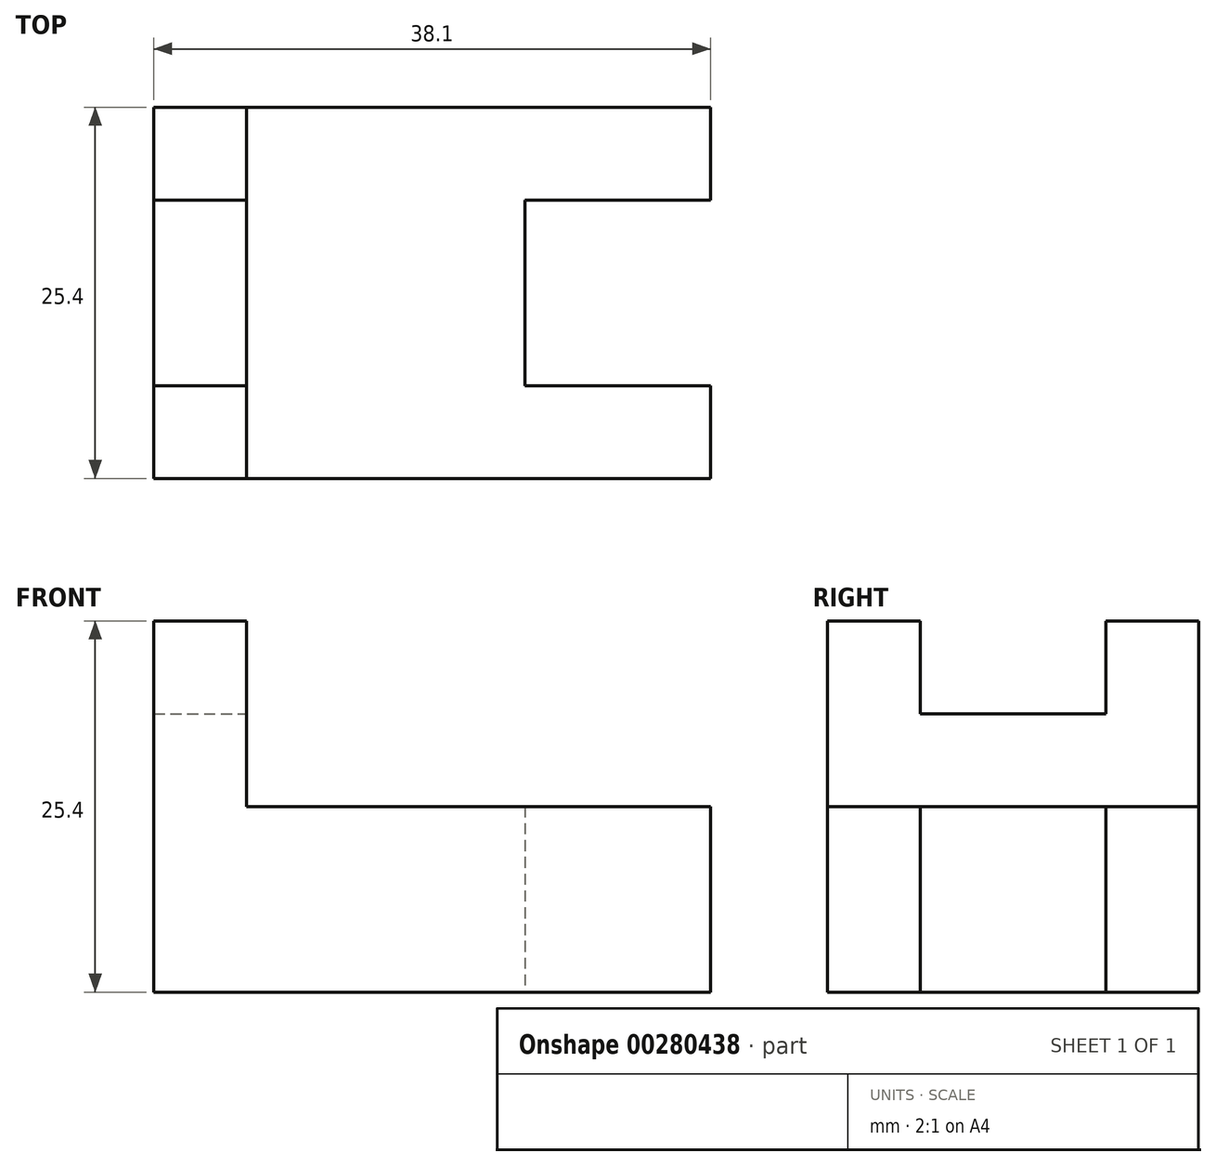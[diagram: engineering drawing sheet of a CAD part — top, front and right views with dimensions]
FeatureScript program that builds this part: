
annotation { "Feature Type Name" : "Feature", "Feature Type Description" : "" }
export const myFeature = defineFeature(function(context is Context, id is Id, definition is map)
    precondition{}
    {
        {
            var Q0;
            Q0=qCreatedBy(makeId("Front.planeOp"),FACE);
            var sketch = newSketch(context, id + "F0", { "sketchPlane" : qUnion([Q0])});
            skLineSegment(sketch, "E0.bottom", {"start": v(0, 25.4) * mm, "end": v(38.1, 25.4) * mm});
            skLineSegment(sketch, "E0.top", {"start": v(0, 0) * mm, "end": v(38.1, 0) * mm});
            skLineSegment(sketch, "E0.left", {"start": v(0, 25.4) * mm, "end": v(0, 0) * mm});
            skLineSegment(sketch, "E0.right", {"start": v(38.1, 25.4) * mm, "end": v(38.1, 0) * mm});
            skSolve(sketch);
        }
        {
            var Q0;
            Q0 = qSketchRegion(id + "F0", true);
            extrude(context, id + "F1", {"entities" : qUnion([Q0]), "endBound" : BoundingType.SYMMETRIC, "depth" : 25.4 * mm});
        }
        {
            var Q0;
            Q0=qCreatedBy(makeId("Front.planeOp"),FACE);
            var sketch = newSketch(context, id + "F2", { "sketchPlane" : qUnion([Q0])});
            skLineSegment(sketch, "E1.bottom", {"start": v(6.35, 25.4) * mm, "end": v(38.1, 25.4) * mm});
            skLineSegment(sketch, "E1.top", {"start": v(6.35, 12.7) * mm, "end": v(38.1, 12.7) * mm});
            skLineSegment(sketch, "E1.left", {"start": v(6.35, 25.4) * mm, "end": v(6.35, 12.7) * mm});
            skLineSegment(sketch, "E1.right", {"start": v(38.1, 25.4) * mm, "end": v(38.1, 12.7) * mm});
            skSolve(sketch);
        }
        {
            var Q0;
            Q0 = qSketchRegion(id + "F2", true);
            extrude(context, id + "F3", {"entities" : qUnion([Q0]), "operationType" : NewBodyOperationType.REMOVE, "endBound" : BoundingType.SYMMETRIC, "oppositeDirection" : true, "depth" : 25.4 * mm});
        }
        {
            var Q0;
            Q0=qCreatedBy(makeId("Front.planeOp"),FACE);
            var sketch = newSketch(context, id + "F4", { "sketchPlane" : qUnion([Q0])});
            skLineSegment(sketch, "E2.bottom", {"start": v(0, 25.4) * mm, "end": v(6.35, 25.4) * mm});
            skLineSegment(sketch, "E2.top", {"start": v(0, 19.05) * mm, "end": v(6.35, 19.05) * mm});
            skLineSegment(sketch, "E2.left", {"start": v(0, 25.4) * mm, "end": v(0, 19.05) * mm});
            skLineSegment(sketch, "E2.right", {"start": v(6.35, 25.4) * mm, "end": v(6.35, 19.05) * mm});
            skSolve(sketch);
        }
        {
            var Q0;
            Q0 = qSketchRegion(id + "F4", true);
            extrude(context, id + "F5", {"entities" : qUnion([Q0]), "operationType" : NewBodyOperationType.REMOVE, "endBound" : BoundingType.SYMMETRIC, "depth" : 12.7 * mm});
        }
        {
            var Q0;
            Q0=qCreatedBy(makeId("Front.planeOp"),FACE);
            var sketch = newSketch(context, id + "F6", { "sketchPlane" : qUnion([Q0])});
            skLineSegment(sketch, "E3.bottom", {"start": v(25.4, 12.7) * mm, "end": v(38.1, 12.7) * mm});
            skLineSegment(sketch, "E3.top", {"start": v(25.4, 0) * mm, "end": v(38.1, 0) * mm});
            skLineSegment(sketch, "E3.left", {"start": v(25.4, 12.7) * mm, "end": v(25.4, 0) * mm});
            skLineSegment(sketch, "E3.right", {"start": v(38.1, 12.7) * mm, "end": v(38.1, 0) * mm});
            skSolve(sketch);
        }
        {
            var Q0;
            Q0 = qSketchRegion(id + "F6", true);
            extrude(context, id + "F7", {"entities" : qUnion([Q0]), "operationType" : NewBodyOperationType.REMOVE, "endBound" : BoundingType.SYMMETRIC, "oppositeDirection" : true, "depth" : 12.7 * mm});
        }
    });
